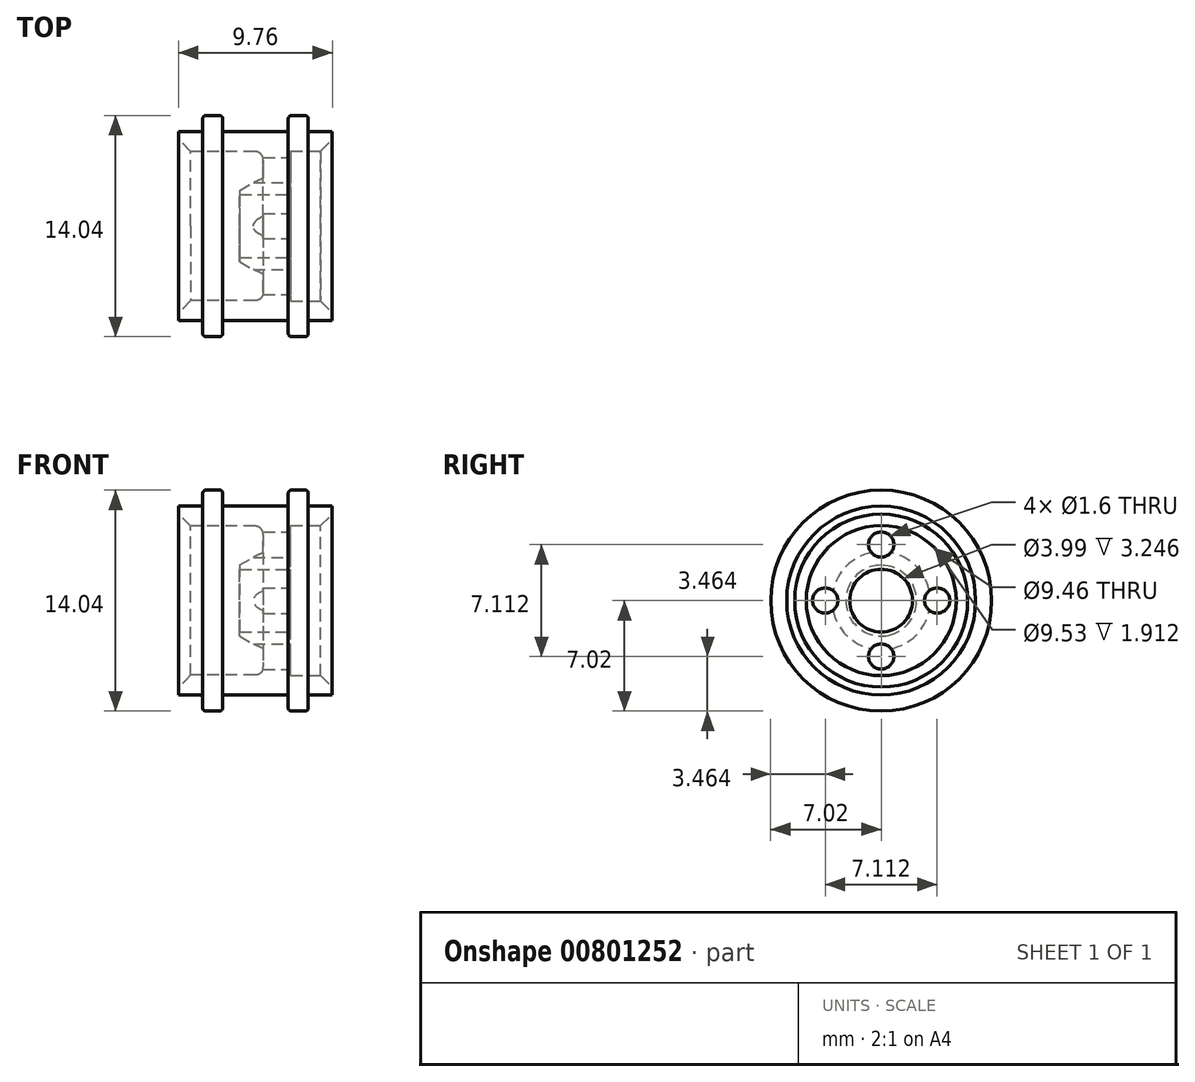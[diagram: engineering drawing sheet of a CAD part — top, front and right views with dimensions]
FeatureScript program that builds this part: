
annotation { "Feature Type Name" : "Feature", "Feature Type Description" : "" }
export const myFeature = defineFeature(function(context is Context, id is Id, definition is map)
    precondition{}
    {
        {
            var Q0;
            Q0=qCreatedBy(makeId("Front.planeOp"),FACE);
            var sketch = newSketch(context, id + "F0", { "sketchPlane" : qUnion([Q0])});
            skLineSegment(sketch, "E0", {"start": v(-1.01, 1) * mm, "end": v(2.49, 1) * mm});
            skLineSegment(sketch, "E1", {"start": v(2.49, 1) * mm, "end": v(2.49, 4.23) * mm});
            skLineSegment(sketch, "E2", {"start": v(2.99, 4.73) * mm, "end": v(4.87, 4.73) * mm});
            skLineSegment(sketch, "E3", {"start": v(4.87, 4.73) * mm, "end": v(4.87, 6) * mm});
            skLineSegment(sketch, "E4", {"start": v(4.87, 6) * mm, "end": v(3.35, 6) * mm});
            skLineSegment(sketch, "E5", {"start": v(3.35, 6) * mm, "end": v(3.35, 7.02) * mm});
            skLineSegment(sketch, "E6", {"start": v(3.35, 7.02) * mm, "end": v(2.08, 7.02) * mm});
            skLineSegment(sketch, "E7", {"start": v(-3.35, 7.02) * mm, "end": v(-3.35, 6) * mm});
            skLineSegment(sketch, "E8", {"start": v(-3.35, 6) * mm, "end": v(-4.87, 6) * mm});
            skLineSegment(sketch, "E9", {"start": v(-4.87, 6) * mm, "end": v(-4.87, 4.73) * mm});
            skLineSegment(sketch, "E10", {"start": v(0.49, 3.12) * mm, "end": v(-1.01, 2.25) * mm});
            skLineSegment(sketch, "E11", {"start": v(-1.01, 2.25) * mm, "end": v(-1.01, 1) * mm});
            skLineSegment(sketch, "E12", {"start": v(0, 7.02) * mm, "end": v(0, 0) * mm, "construction": true});
            skLineSegment(sketch, "E13", {"start": v(0, 0) * mm, "end": v(34.63, 0) * mm});
            skLineSegment(sketch, "E14.left", {"start": v(-2.08, 7.02) * mm, "end": v(-2.08, 6) * mm});
            skLineSegment(sketch, "E14.right", {"start": v(2.08, 7.02) * mm, "end": v(2.08, 6) * mm});
            skLineSegment(sketch, "E15.trimOffspring", {"start": v(-2.08, 7.02) * mm, "end": v(-3.35, 7.02) * mm});
            skLineSegment(sketch, "E16", {"start": v(0.49, 3.12) * mm, "end": v(0.49, 4.23) * mm});
            skArc(sketch, "E17.filletArc", {"start": v(0.49, 4.23) * mm, "mid": v(0.34, 4.58) * mm, "end": v(-0.01, 4.73) * mm});
            skLineSegment(sketch, "E18", {"start": v(2.49, 4.23) * mm, "end": v(2.99, 4.73) * mm});
            skLineSegment(sketch, "E19", {"start": v(-2.08, 6) * mm, "end": v(2.08, 6) * mm});
            skLineSegment(sketch, "E20", {"start": v(-4.87, 5.37) * mm, "end": v(0, 5.37) * mm, "construction": true});
            skLineSegment(sketch, "E21", {"start": v(0, 5.37) * mm, "end": v(4.87, 5.37) * mm, "construction": true});
            skLineSegment(sketch, "E22", {"start": v(-2.08, 7.02) * mm, "end": v(0, 7.02) * mm, "construction": true});
            skLineSegment(sketch, "E23", {"start": v(0, 7.02) * mm, "end": v(2.08, 7.02) * mm, "construction": true});
            skLineSegment(sketch, "E24", {"start": v(-4.87, 4.73) * mm, "end": v(-0.01, 4.73) * mm});
            skSolve(sketch);
        }
        {
            var Q0;
            Q0=qSketchRegion(id+"F0",true);
            var Q1;
            Q1=sQuery(id+"F0.wireOp",EDGE,"E13");
            revolve(context, id + "F1", {"surfaceOperationType" : NewSurfaceOperationType.NEW, "entities" : qUnion([Q0]), "axis" : qUnion([Q1]), "revolveType" : RevolveType.FULL});
        }
        {
            var Q0;
            Q0=makeQuery(id+"F1.opRevolve","SWEPT_EDGE",EDGE,{"disambiguationData":[OSD([sQuery(id+"F0.wireOp",EDGE,"E5"),sQuery(id+"F0.wireOp",EDGE,"E6")])]});
            var Q1;
            Q1=makeQuery(id+"F1.opRevolve","SWEPT_EDGE",EDGE,{"disambiguationData":[OSD([sQuery(id+"F0.wireOp",EDGE,"E6"),sQuery(id+"F0.wireOp",EDGE,"E7")])]});
            var Q2;
            Q2=makeQuery(id+"F1.opRevolve","SWEPT_EDGE",EDGE,{"disambiguationData":[OSD([sQuery(id+"F0.wireOp",EDGE,"E14.left"),sQuery(id+"F0.wireOp",EDGE,"E15.trimOffspring")])]});
            fillet(context, id + "F2", {"entities" : qUnion([Q0, Q1, Q2]), "radius" : 0.2 * mm, "tangentPropagation" : true, "allowEdgeOverflow" : false});
        }
        {
            var Q0;
            Q0=makeQuery(id+"F1.opRevolve","SWEPT_EDGE",EDGE,{"disambiguationData":[OSD([sQuery(id+"F0.wireOp",EDGE,"E2"),sQuery(id+"F0.wireOp",EDGE,"E3")])]});
            var Q1;
            Q1=makeQuery(id+"F1.opRevolve","SWEPT_EDGE",EDGE,{"disambiguationData":[OSD([sQuery(id+"F0.wireOp",EDGE,"E9"),sQuery(id+"F0.wireOp",EDGE,"E24")])]});
            chamfer(context, id + "F3", {"entities" : qUnion([Q0, Q1]), "width" : 0.76 * mm, "tangentPropagation" : true});
        }
        {
            var Q0;
            Q0=makeQuery(id+"F1.opRevolve","SWEPT_FACE",FACE,{"disambiguationData":[OSD([sQuery(id+"F0.wireOp",EDGE,"E1")])]});
            var sketch = newSketch(context, id + "F4", { "sketchPlane" : qUnion([Q0])});
            skCircle(sketch, "E25.cCircle", {"center": v(0, 0) * mm, "radius": 3.17 * mm, "construction": true});
            skLineSegment(sketch, "E25.0", {"start": v(3.18, -1.83) * mm, "end": v(0, -3.67) * mm, "construction": true});
            skLineSegment(sketch, "E25.1", {"start": v(0, -3.67) * mm, "end": v(-3.18, -1.83) * mm, "construction": true});
            skLineSegment(sketch, "E25.2", {"start": v(-3.17, -1.83) * mm, "end": v(-3.17, 1.83) * mm, "construction": true});
            skLineSegment(sketch, "E25.3", {"start": v(-3.18, 1.83) * mm, "end": v(0, 3.67) * mm, "construction": true});
            skLineSegment(sketch, "E25.4", {"start": v(0, 3.67) * mm, "end": v(3.17, 1.83) * mm, "construction": true});
            skLineSegment(sketch, "E25.5", {"start": v(3.17, 1.83) * mm, "end": v(3.17, -1.83) * mm, "construction": true});
            skPoint(sketch, "E25.0.midPoint", {"position": v(1.59, -2.75) * mm});
            skCircle(sketch, "E26", {"center": v(0, 3.56) * mm, "radius": 0.8 * mm});
            skCircle(sketch, "E27", {"center": v(0, -3.56) * mm, "radius": 0.8 * mm});
            skCircle(sketch, "E28", {"center": v(0, 0) * mm, "radius": 3.56 * mm, "construction": true});
            skCircle(sketch, "E29", {"center": v(-3.56, 0) * mm, "radius": 0.8 * mm});
            skCircle(sketch, "E30", {"center": v(3.56, 0) * mm, "radius": 0.8 * mm});
            skCircle(sketch, "E31", {"center": v(0, 0) * mm, "radius": 2 * mm});
            skSolve(sketch);
        }
        {
            var Q0;
            Q0 = qSketchRegion(id + "F4", true);
            extrude(context, id + "F5", {"entities" : qUnion([Q0]), "operationType" : NewBodyOperationType.REMOVE, "endBound" : BoundingType.THROUGH_ALL, "oppositeDirection" : true, "depth" : 25.4 * mm, "offsetDistance" : 25.4 * mm});
        }
        {
            var Q0;
            Q0=makeQuery(id+"F1.opRevolve","SWEPT_FACE",FACE,{"disambiguationData":[OSD([sQuery(id+"F0.wireOp",EDGE,"E1")])]});
            var sketch = newSketch(context, id + "F6", { "sketchPlane" : qUnion([Q0])});
            skCircle(sketch, "E32", {"center": v(0, 0) * mm, "radius": 4.76 * mm});
            skSolve(sketch);
        }
        {
            var Q0;
            Q0 = qSketchRegion(id + "F6", true);
            extrude(context, id + "F7", {"entities" : qUnion([Q0]), "operationType" : NewBodyOperationType.REMOVE, "oppositeDirection" : true, "depth" : 0.25 * mm, "offsetDistance" : 25.4 * mm, "hasSecondDirection" : true, "secondDirectionBound" : BoundingType.THROUGH_ALL, "secondDirectionOppositeDirection" : false, "secondDirectionDepth" : 25.4 * mm});
        }
    });
